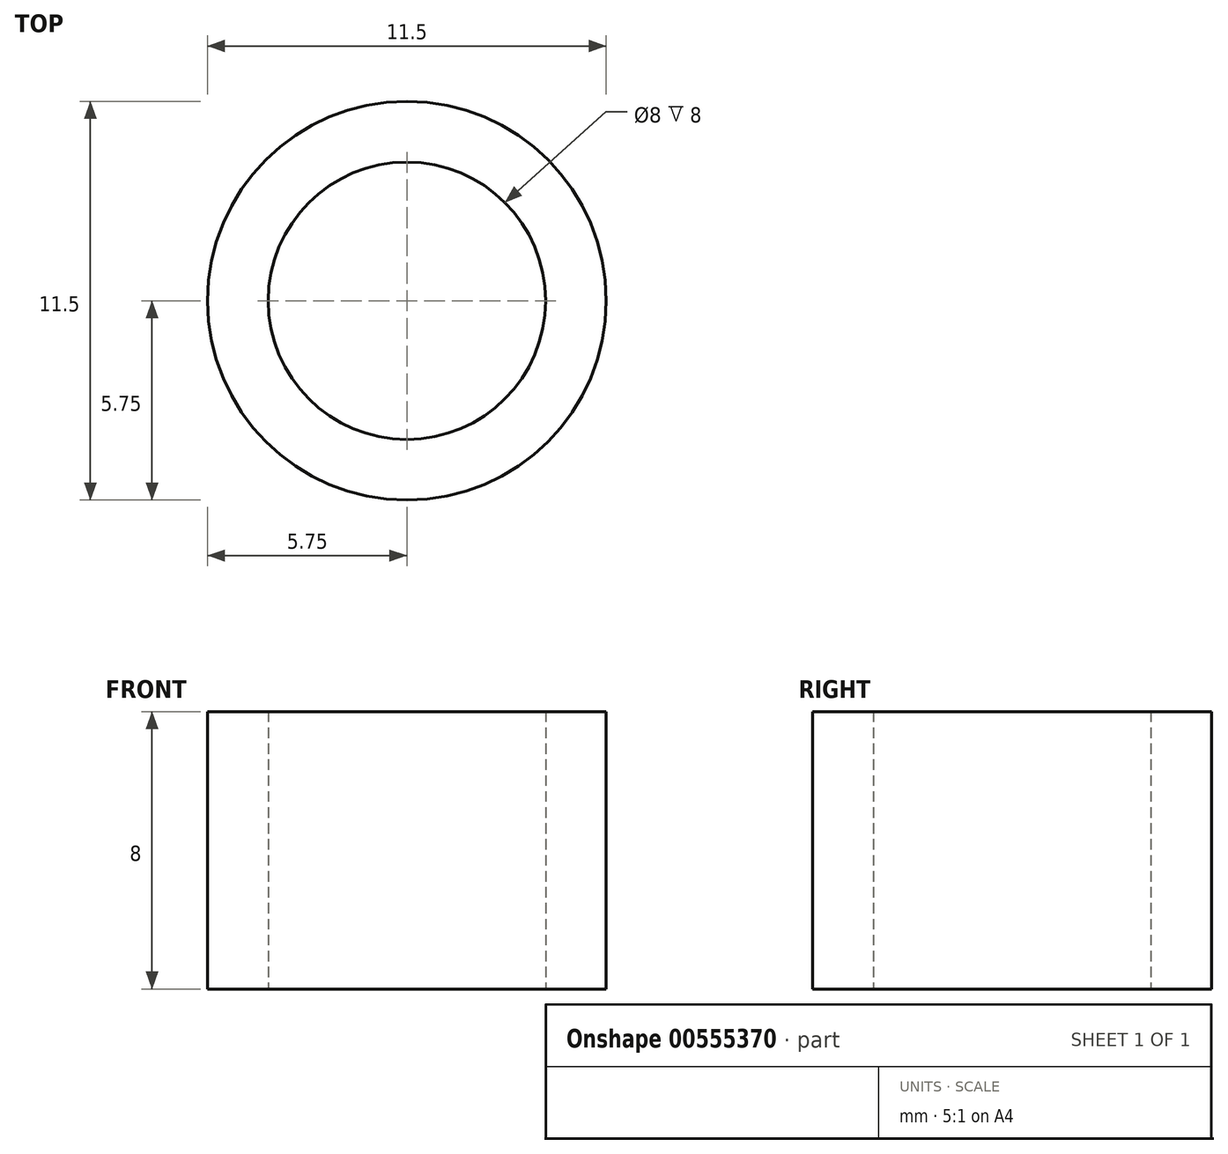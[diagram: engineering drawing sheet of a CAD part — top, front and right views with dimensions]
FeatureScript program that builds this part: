
annotation { "Feature Type Name" : "Feature", "Feature Type Description" : "" }
export const myFeature = defineFeature(function(context is Context, id is Id, definition is map)
    precondition{}
    {
        {
            var Q0;
            Q0=qCreatedBy(makeId("Top.planeOp"),FACE);
            var sketch = newSketch(context, id + "F0", { "sketchPlane" : qUnion([Q0])});
            skCircle(sketch, "E0", {"center": v(0, 0) * mm, "radius": 5.75 * mm});
            skSolve(sketch);
        }
        {
            var Q0;
            Q0=makeQuery(id+"F0.imprint","IMPRINT",FACE,{"disambiguationData":[TD([[makeQuery(id+"F0.imprint","IMPRINT",EDGE,{"derivedFrom":sQuery(id+"F0.wireOp",EDGE,"E0")}),1.0]])]});
            var sketch = newSketch(context, id + "F1", { "sketchPlane" : qUnion([Q0])});
            skCircle(sketch, "E1", {"center": v(0, 0) * mm, "radius": 4 * mm});
            skSolve(sketch);
        }
        {
            var Q0;
            Q0=makeQuery(id+"F1.imprint","IMPRINT",FACE,{"disambiguationData":[TD([[makeQuery(id+"F1.imprint","IMPRINT",EDGE,{"derivedFrom":sQuery(id+"F1.wireOp",EDGE,"E1")}),-1.0]])]});
            extrude(context, id + "F2", {"entities" : qUnion([Q0]), "depth" : 8 * mm, "offsetDistance" : 25 * mm});
        }
    });
